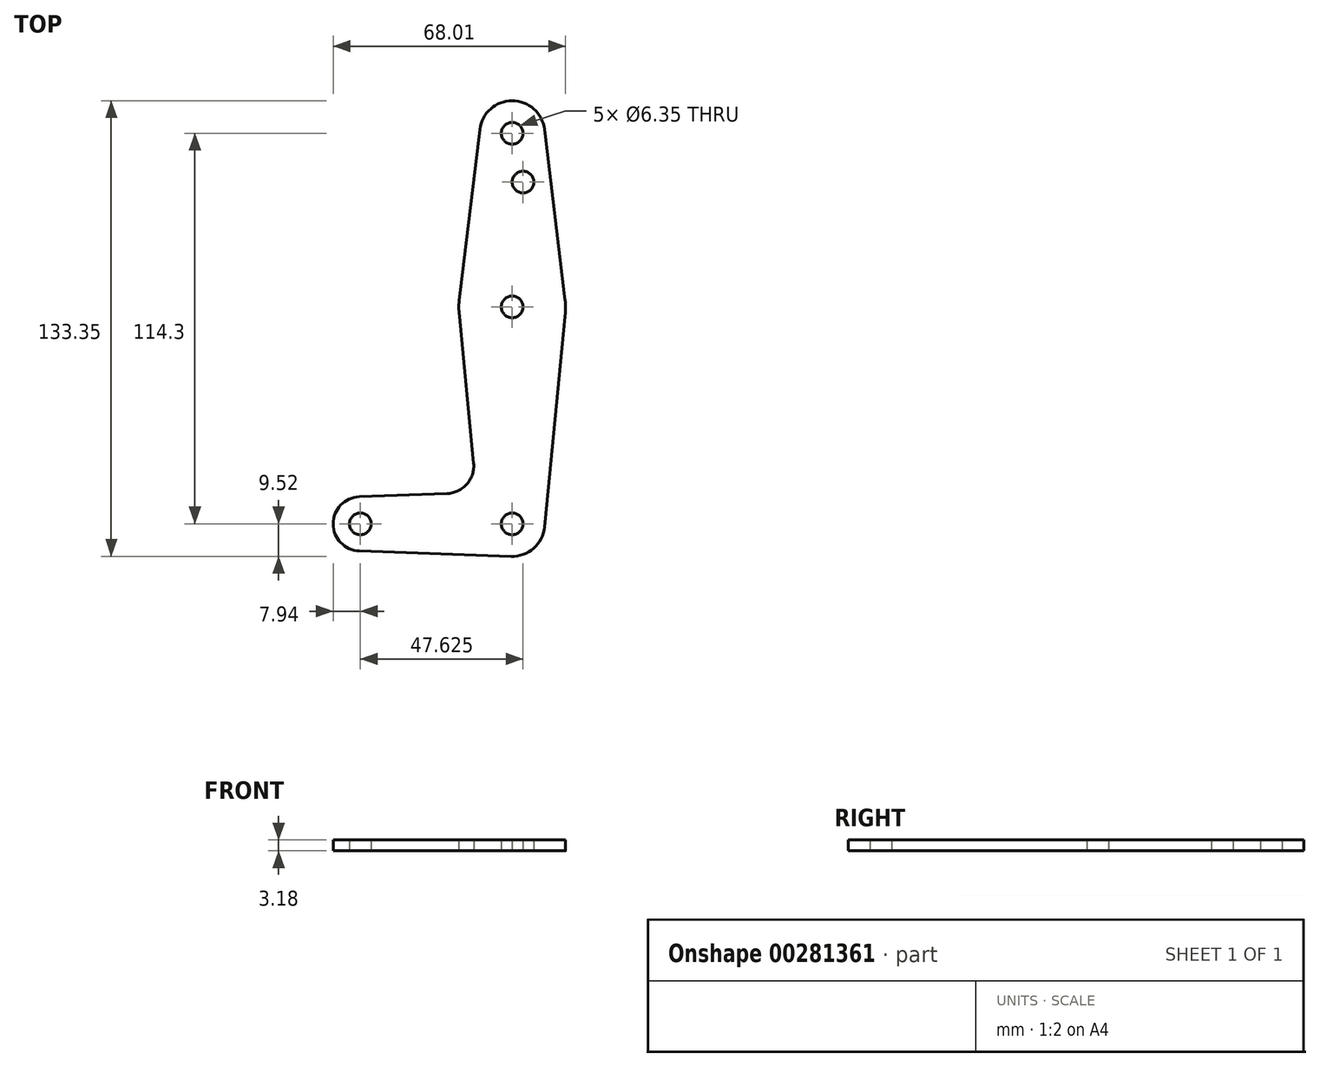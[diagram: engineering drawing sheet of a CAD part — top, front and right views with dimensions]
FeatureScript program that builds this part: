
annotation { "Feature Type Name" : "Feature", "Feature Type Description" : "" }
export const myFeature = defineFeature(function(context is Context, id is Id, definition is map)
    precondition{}
    {
        {
            var Q0;
            Q0=qCreatedBy(makeId("Top.planeOp"),FACE);
            var sketch = newSketch(context, id + "F0", { "sketchPlane" : qUnion([Q0])});
            skCircle(sketch, "E0", {"center": v(0, 0) * mm, "radius": 3.17 * mm});
            skCircle(sketch, "E1", {"center": v(-44.45, 0) * mm, "radius": 3.18 * mm});
            skCircle(sketch, "E2", {"center": v(0, 63.5) * mm, "radius": 3.18 * mm});
            skCircle(sketch, "E3", {"center": v(0, 114.3) * mm, "radius": 3.18 * mm});
            skCircle(sketch, "E4", {"center": v(0, 0) * mm, "radius": 9.53 * mm});
            skCircle(sketch, "E5", {"center": v(-44.45, 0) * mm, "radius": 7.94 * mm});
            skCircle(sketch, "E6", {"center": v(0, 63.5) * mm, "radius": 15.62 * mm});
            skCircle(sketch, "E7", {"center": v(0, 114.3) * mm, "radius": 9.53 * mm});
            skLineSegment(sketch, "E8", {"start": v(9.48, -0.91) * mm, "end": v(15.55, 62) * mm});
            skLineSegment(sketch, "E9", {"start": v(9.46, 115.44) * mm, "end": v(15.5, 65.37) * mm});
            skLineSegment(sketch, "E10", {"start": v(-9.46, 115.44) * mm, "end": v(-15.5, 65.37) * mm});
            skLineSegment(sketch, "E11", {"start": v(-15.87, 65.37) * mm, "end": v(-11.29, 17.82) * mm});
            skLineSegment(sketch, "E12", {"start": v(-44.73, 7.93) * mm, "end": v(-19.15, 8.85) * mm});
            skLineSegment(sketch, "E13", {"start": v(-44.73, -7.93) * mm, "end": v(-0.34, -9.52) * mm});
            skLineSegment(sketch, "E14.trimOffspring", {"start": v(-0.34, 9.52) * mm, "end": v(0, 9.53) * mm});
            skArc(sketch, "E15.filletArc", {"start": v(-19.15, 8.85) * mm, "mid": v(-13.28, 11.63) * mm, "end": v(-11.29, 17.82) * mm});
            skLineSegment(sketch, "E16", {"start": v(0, 114.3) * mm, "end": v(0, 0) * mm, "construction": true});
            skCircle(sketch, "E17", {"center": v(3.17, 100.01) * mm, "radius": 3.18 * mm});
            skSolve(sketch);
        }
        {
            var Q0;
            Q0 = qSketchRegion(id + "F0", true);
            extrude(context, id + "F1", {"entities" : qUnion([Q0]), "depth" : 3.17 * mm});
        }
    });
